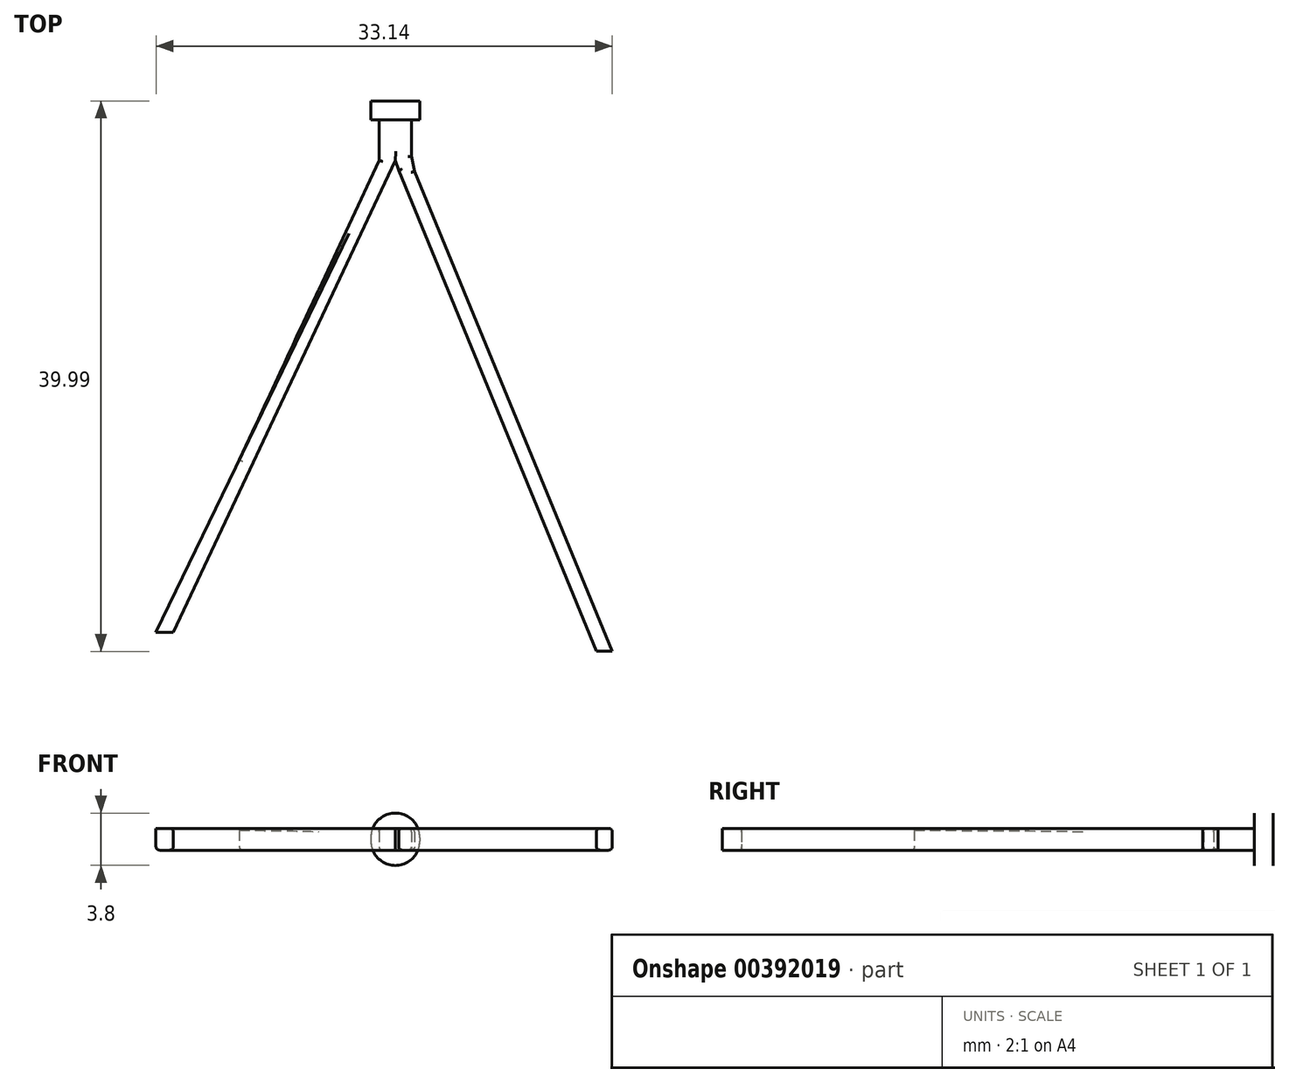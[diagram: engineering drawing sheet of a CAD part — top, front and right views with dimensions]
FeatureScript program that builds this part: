
annotation { "Feature Type Name" : "Feature", "Feature Type Description" : "" }
export const myFeature = defineFeature(function(context is Context, id is Id, definition is map)
    precondition{}
    {
        {
            var Q0;
            Q0=qCreatedBy(makeId("Top.planeOp"),FACE);
            var sketch = newSketch(context, id + "F0", { "sketchPlane" : qUnion([Q0])});
            skCircle(sketch, "E0", {"center": v(0, 0) * mm, "radius": 43.07 * mm});
            skCircle(sketch, "E1", {"center": v(0, 0) * mm, "radius": 31.97 * mm});
            skSolve(sketch);
        }
        {
            var Q0;
            Q0=qCreatedBy(makeId("Top.planeOp"),FACE);
            var sketch = newSketch(context, id + "F1", { "sketchPlane" : qUnion([Q0])});
            skLineSegment(sketch, "E2", {"start": v(-2.9, 19.79) * mm, "end": v(-6.96, 11.11) * mm});
            skLineSegment(sketch, "E3", {"start": v(-1.73, 19.76) * mm, "end": v(-5.7, 11.32) * mm});
            skLineSegment(sketch, "E4", {"start": v(-1.14, 19.77) * mm, "end": v(13.22, -15.18) * mm});
            skLineSegment(sketch, "E5", {"start": v(13.22, -15.18) * mm, "end": v(14.37, -15.18) * mm});
            skLineSegment(sketch, "E6", {"start": v(14.37, -15.18) * mm, "end": v(0, 19.7) * mm});
            skLineSegment(sketch, "E7", {"start": v(-18.77, -13.8) * mm, "end": v(-12.72, -1.25) * mm});
            skLineSegment(sketch, "E8", {"start": v(-5.7, 11.32) * mm, "end": v(-11.97, -2) * mm});
            skLineSegment(sketch, "E9", {"start": v(-11.97, -2) * mm, "end": v(-17.52, -13.8) * mm});
            skLineSegment(sketch, "E10", {"start": v(-17.52, -13.8) * mm, "end": v(-18.77, -13.8) * mm});
            skLineSegment(sketch, "E11", {"start": v(-2.9, 19.79) * mm, "end": v(-2.57, 20.49) * mm});
            skLineSegment(sketch, "E12", {"start": v(-2.57, 20.49) * mm, "end": v(-2.57, 22.09) * mm});
            skLineSegment(sketch, "E13", {"start": v(-2.57, 22.09) * mm, "end": v(-2.57, 23.44) * mm});
            skLineSegment(sketch, "E14", {"start": v(-2.57, 23.44) * mm, "end": v(-3.16, 23.44) * mm});
            skLineSegment(sketch, "E15", {"start": v(-3.16, 23.44) * mm, "end": v(-3.16, 24.81) * mm});
            skLineSegment(sketch, "E16", {"start": v(-3.16, 24.81) * mm, "end": v(0.38, 24.81) * mm});
            skLineSegment(sketch, "E17", {"start": v(0.38, 24.81) * mm, "end": v(0.38, 23.44) * mm});
            skLineSegment(sketch, "E18", {"start": v(0.38, 23.44) * mm, "end": v(-0.2, 23.44) * mm});
            skLineSegment(sketch, "E19", {"start": v(-0.2, 23.44) * mm, "end": v(-0.2, 22.09) * mm});
            skLineSegment(sketch, "E20", {"start": v(-0.2, 22.09) * mm, "end": v(-0.2, 20.8) * mm});
            skLineSegment(sketch, "E21", {"start": v(-0.2, 20.8) * mm, "end": v(0, 19.7) * mm});
            skLineSegment(sketch, "E22", {"start": v(-1.73, 19.76) * mm, "end": v(-1.39, 20.49) * mm});
            skLineSegment(sketch, "E23", {"start": v(-1.39, 20.49) * mm, "end": v(-1.14, 19.77) * mm});
            skFitSpline(sketch, "E24", {"points": [v(-0.2, 22.09) * mm, v(-1.9, 21.95) * mm, v(-2.57, 22.09) * mm], "startDerivative": vector(-0.4, -0.49) * mm, "endDerivative": vector(-1.4, 0.4) * mm});
            skFitSpline(sketch, "E25", {"points": [v(-2.9, 19.79) * mm, v(-2.46, 19.73) * mm, v(-1.73, 19.76) * mm], "startDerivative": vector(0.82, -0.23) * mm, "endDerivative": vector(1.62, 0.2) * mm});
            skFitSpline(sketch, "E26", {"points": [v(-1.14, 19.77) * mm, v(-0.43, 19.77) * mm, v(0, 19.7) * mm], "startDerivative": vector(1.35, 0.05) * mm, "endDerivative": vector(0.93, -0.2) * mm});
            skFitSpline(sketch, "E27", {"points": [v(-5.7, 11.32) * mm, v(-6.38, 11.22) * mm, v(-6.96, 11.11) * mm], "startDerivative": vector(-1.31, -0.16) * mm, "endDerivative": vector(-1.19, -0.27) * mm});
            skFitSpline(sketch, "E28", {"points": [v(-12.72, -1.25) * mm, v(-12.32, -1.64) * mm, v(-11.97, -2) * mm], "startDerivative": vector(0.39, -0.42) * mm, "endDerivative": vector(0.39, -0.42) * mm});
            skLineSegment(sketch, "E29", {"start": v(-1.39, 24.81) * mm, "end": v(-1.39, 20.49) * mm, "construction": true});
            skLineSegment(sketch, "E30", {"start": v(-2.57, 23.44) * mm, "end": v(-1.39, 23.44) * mm});
            skLineSegment(sketch, "E31", {"start": v(-1.39, 23.44) * mm, "end": v(-0.2, 23.44) * mm});
            skLineSegment(sketch, "E32", {"start": v(-12.72, -1.25) * mm, "end": v(-6.96, 11.11) * mm});
            skSolve(sketch);
        }
        {
            var Q0;
            Q0=makeQuery(id+"F1.imprint","IMPRINT",FACE,{"disambiguationData":[TD([[makeQuery(id+"F1.imprint","IMPRINT",EDGE,{"derivedFrom":sQuery(id+"F1.wireOp",EDGE,"E2")}),1.0]])]});
            var Q1;
            Q1=makeQuery(id+"F1.imprint","IMPRINT",FACE,{"disambiguationData":[TD([[makeQuery(id+"F1.imprint","IMPRINT",EDGE,{"derivedFrom":sQuery(id+"F1.wireOp",EDGE,"E8")}),-1.0]])]});
            var Q2;
            Q2=makeQuery(id+"F1.imprint","IMPRINT",FACE,{"disambiguationData":[TD([[makeQuery(id+"F1.imprint","IMPRINT",EDGE,{"derivedFrom":sQuery(id+"F1.wireOp",EDGE,"E4")}),1.0]])]});
            var Q3;
            Q3=makeQuery(id+"F1.imprint","IMPRINT",FACE,{"disambiguationData":[TD([[makeQuery(id+"F1.imprint","IMPRINT",EDGE,{"derivedFrom":sQuery(id+"F1.wireOp",EDGE,"E11")}),-1.0]])]});
            var Q4;
            Q4=makeQuery(id+"F1.imprint","IMPRINT",FACE,{"disambiguationData":[TD([[makeQuery(id+"F1.imprint","IMPRINT",EDGE,{"derivedFrom":sQuery(id+"F1.wireOp",EDGE,"E13")}),-1.0]])]});
            var Q5;
            Q5=makeQuery(id+"F1.imprint","IMPRINT",FACE,{"disambiguationData":[TD([[makeQuery(id+"F1.imprint","IMPRINT",EDGE,{"derivedFrom":sQuery(id+"F1.wireOp",EDGE,"E7")}),-1.0]])]});
            extrude(context, id + "F2", {"entities" : qUnion([Q0, Q1, Q2, Q3, Q4, Q5]), "endBound" : BoundingType.SYMMETRIC, "depth" : 1.59 * mm});
        }
        {
            var Q0;
            Q0=makeQuery(id+"F1.imprint","IMPRINT",FACE,{"disambiguationData":[TD([[makeQuery(id+"F1.imprint","IMPRINT",EDGE,{"derivedFrom":sQuery(id+"F1.wireOp",EDGE,"E14")}),-1.0]])]});
            extrude(context, id + "F3", {"entities" : qUnion([Q0]), "operationType" : NewBodyOperationType.ADD, "endBound" : BoundingType.SYMMETRIC, "depth" : 3.8 * mm});
        }
        {
            var Q0;
            Q0=makeQuery(id+"F3.opExtrude","CAP_EDGE",EDGE,{"disambiguationData":[OSD([sQuery(id+"F1.wireOp",EDGE,"E15")])],"isStart":false});
            var Q1;
            Q1=makeQuery(id+"F3.opExtrude","CAP_EDGE",EDGE,{"disambiguationData":[OSD([sQuery(id+"F1.wireOp",EDGE,"E17")])],"isStart":false});
            var Q2;
            Q2=makeQuery(id+"F3.opExtrude","CAP_EDGE",EDGE,{"disambiguationData":[OSD([sQuery(id+"F1.wireOp",EDGE,"E17")])],"isStart":true});
            var Q3;
            Q3=makeQuery(id+"F3.opExtrude","CAP_EDGE",EDGE,{"disambiguationData":[OSD([sQuery(id+"F1.wireOp",EDGE,"E15")])],"isStart":true});
            fillet(context, id + "F4", {"entities" : qUnion([Q0, Q1, Q2, Q3]), "radius" : 1.78 * mm, "tangentPropagation" : true, "allowEdgeOverflow" : false});
        }
        {
            var Q0;
            Q0=makeQuery(id+"F2.opExtrude","CAP_EDGE",EDGE,{"disambiguationData":[OSD([sQuery(id+"F1.wireOp",EDGE,"E12"),sQuery(id+"F1.wireOp",EDGE,"E13")])],"isStart":true});
            var Q1;
            Q1=makeQuery(id+"F2.opExtrude","CAP_EDGE",EDGE,{"disambiguationData":[OSD([sQuery(id+"F1.wireOp",EDGE,"E2"),sQuery(id+"F1.wireOp",EDGE,"E11")])],"isStart":true});
            var Q2;
            Q2=makeQuery(id+"F2.opExtrude","CAP_EDGE",EDGE,{"disambiguationData":[OSD([sQuery(id+"F1.wireOp",EDGE,"E32")])],"isStart":true});
            var Q3;
            Q3=makeQuery(id+"F2.opExtrude","CAP_EDGE",EDGE,{"disambiguationData":[OSD([sQuery(id+"F1.wireOp",EDGE,"E7")])],"isStart":true});
            var Q4;
            Q4=makeQuery(id+"F2.opExtrude","CAP_EDGE",EDGE,{"disambiguationData":[OSD([sQuery(id+"F1.wireOp",EDGE,"E6")])],"isStart":true});
            var Q5;
            Q5=makeQuery(id+"F2.opExtrude","CAP_EDGE",EDGE,{"disambiguationData":[OSD([sQuery(id+"F1.wireOp",EDGE,"E21")])],"isStart":true});
            var Q6;
            Q6=makeQuery(id+"F2.opExtrude","CAP_EDGE",EDGE,{"disambiguationData":[OSD([sQuery(id+"F1.wireOp",EDGE,"E19"),sQuery(id+"F1.wireOp",EDGE,"E20")])],"isStart":true});
            var Q7;
            Q7=makeQuery(id+"F2.opExtrude","CAP_EDGE",EDGE,{"disambiguationData":[OSD([sQuery(id+"F1.wireOp",EDGE,"E4")])],"isStart":true});
            var Q8;
            Q8=makeQuery(id+"F2.opExtrude","CAP_EDGE",EDGE,{"disambiguationData":[OSD([sQuery(id+"F1.wireOp",EDGE,"E3"),sQuery(id+"F1.wireOp",EDGE,"E8"),sQuery(id+"F1.wireOp",EDGE,"E9"),sQuery(id+"F1.wireOp",EDGE,"E22")])],"isStart":true});
            var Q9;
            Q9=makeQuery(id+"F2.opExtrude","CAP_EDGE",EDGE,{"disambiguationData":[OSD([sQuery(id+"F1.wireOp",EDGE,"E3"),sQuery(id+"F1.wireOp",EDGE,"E8"),sQuery(id+"F1.wireOp",EDGE,"E9"),sQuery(id+"F1.wireOp",EDGE,"E22")])],"isStart":false});
            var Q10;
            Q10=makeQuery(id+"F2.opExtrude","CAP_EDGE",EDGE,{"disambiguationData":[OSD([sQuery(id+"F1.wireOp",EDGE,"E6")])],"isStart":false});
            var Q11;
            Q11=makeQuery(id+"F2.opExtrude","CAP_EDGE",EDGE,{"disambiguationData":[OSD([sQuery(id+"F1.wireOp",EDGE,"E4")])],"isStart":false});
            var Q12;
            Q12=makeQuery(id+"F2.opExtrude","CAP_EDGE",EDGE,{"disambiguationData":[OSD([sQuery(id+"F1.wireOp",EDGE,"E12"),sQuery(id+"F1.wireOp",EDGE,"E13")])],"isStart":false});
            var Q13;
            Q13=makeQuery(id+"F2.opExtrude","CAP_EDGE",EDGE,{"disambiguationData":[OSD([sQuery(id+"F1.wireOp",EDGE,"E2"),sQuery(id+"F1.wireOp",EDGE,"E11")])],"isStart":false});
            var Q14;
            Q14=makeQuery(id+"F2.opExtrude","CAP_EDGE",EDGE,{"disambiguationData":[OSD([sQuery(id+"F1.wireOp",EDGE,"E19"),sQuery(id+"F1.wireOp",EDGE,"E20")])],"isStart":false});
            var Q15;
            Q15=makeQuery(id+"F2.opExtrude","CAP_EDGE",EDGE,{"disambiguationData":[OSD([sQuery(id+"F1.wireOp",EDGE,"E21")])],"isStart":false});
            var Q16;
            Q16=makeQuery(id+"F2.opExtrude","CAP_EDGE",EDGE,{"disambiguationData":[OSD([sQuery(id+"F1.wireOp",EDGE,"E23")])],"isStart":false});
            var Q17;
            Q17=makeQuery(id+"F2.opExtrude","CAP_EDGE",EDGE,{"disambiguationData":[OSD([sQuery(id+"F1.wireOp",EDGE,"E23")])],"isStart":true});
            fillet(context, id + "F5", {"entities" : qUnion([Q0, Q1, Q2, Q3, Q4, Q5, Q6, Q7, Q8, Q9, Q10, Q11, Q12, Q13, Q14, Q15, Q16, Q17]), "radius" : 0.25 * mm, "tangentPropagation" : true, "allowEdgeOverflow" : false});
        }
    });
